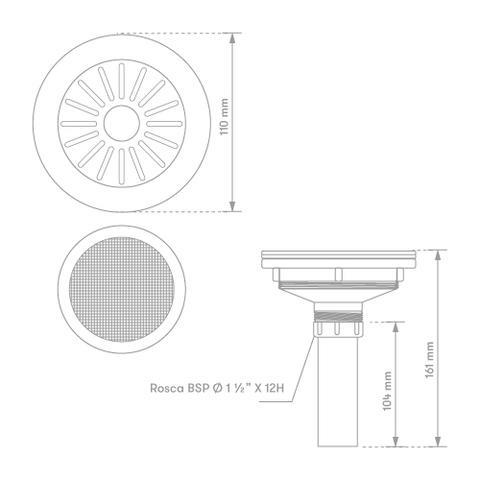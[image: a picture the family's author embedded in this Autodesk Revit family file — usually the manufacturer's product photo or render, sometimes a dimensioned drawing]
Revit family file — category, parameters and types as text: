
# Revit family: BIM_TB-1954-11S
name_source: partatom
category: Plumbing Fixtures
units: mm (PartAtom-declared; Revit-internal decimal feet)

## family parameters
Classification Number = 23.31.11.00
Cut with Voids When Loaded = No
Enable Cutting in Views = No
Host = Face
Maintain Annotation Orientation = No
Part Type = Normal
Room Calculation Point = No
Round Connector Dimension = Use Diameter
Shared = No

## types (1)
- TB-1954-11S
    Alto = 140 mm  [stored 0.459318 ft]
    CW Connection = Yes
    Caucho = Plastico - polipropileno + colorante gris
    Caudal = 27 l/m
    Conexiones = Tubo para acople en tubería de 1½”
    Date Modified = 22/08/2025
    Default Elevation = 0 mm  [stored 0 ft]
    Description = Canastilla
    Diametro = 74.3 mm
    Garantia Especifica = 20 Años
    Goteo de sello = 63 ml/min
    HW Connection = Yes
    Link Ficha Tecnica = https://infotecnica.gricol.com
    Manufacturer = Gricol
    Materiales del producto = ABS, Popilipropileno, Acero inoxidable,
Caucho
    Medida Externa = 1 1/2"
    Metal - Acero inoxidable = Metal - Acero inoxidable
    Model = TB-1954-11S
    Plastico - polipropileno + colorante blanco = Plastico - polipropileno + colorante blanco
    Product Name = Canastilla 2 Inoxidable Para Lavaplatos
    Referente Normativo = NTC 5302, ASME A112.18.2 / CSA B125.2
    Resistencia a Corrosión = NTC 1156, Sal Neutral
    Sitio web = https://www.gricol.com
    Temperaturas de trabajo = 19C° A 62C°
    Tipo de Uso = Domestico
    Torque de Conexioón = 20 Nm
    Type Image = FOTO CANASTILLA 2 CON FILTRO INOXIDABLE.jpg
    URL = https://www.gricol.com
    Vent Connection = No
    Vida Util = 100000 Ciclos
    Waste Connection = No

note: [stored X ft] marks values corroborated as IEEE doubles in the binary element streams (Revit-internal decimal feet)

## geometry (parser evidence)
native form markers: Blend x2, Sweep x3
no freeform markers — native parametric forms only
